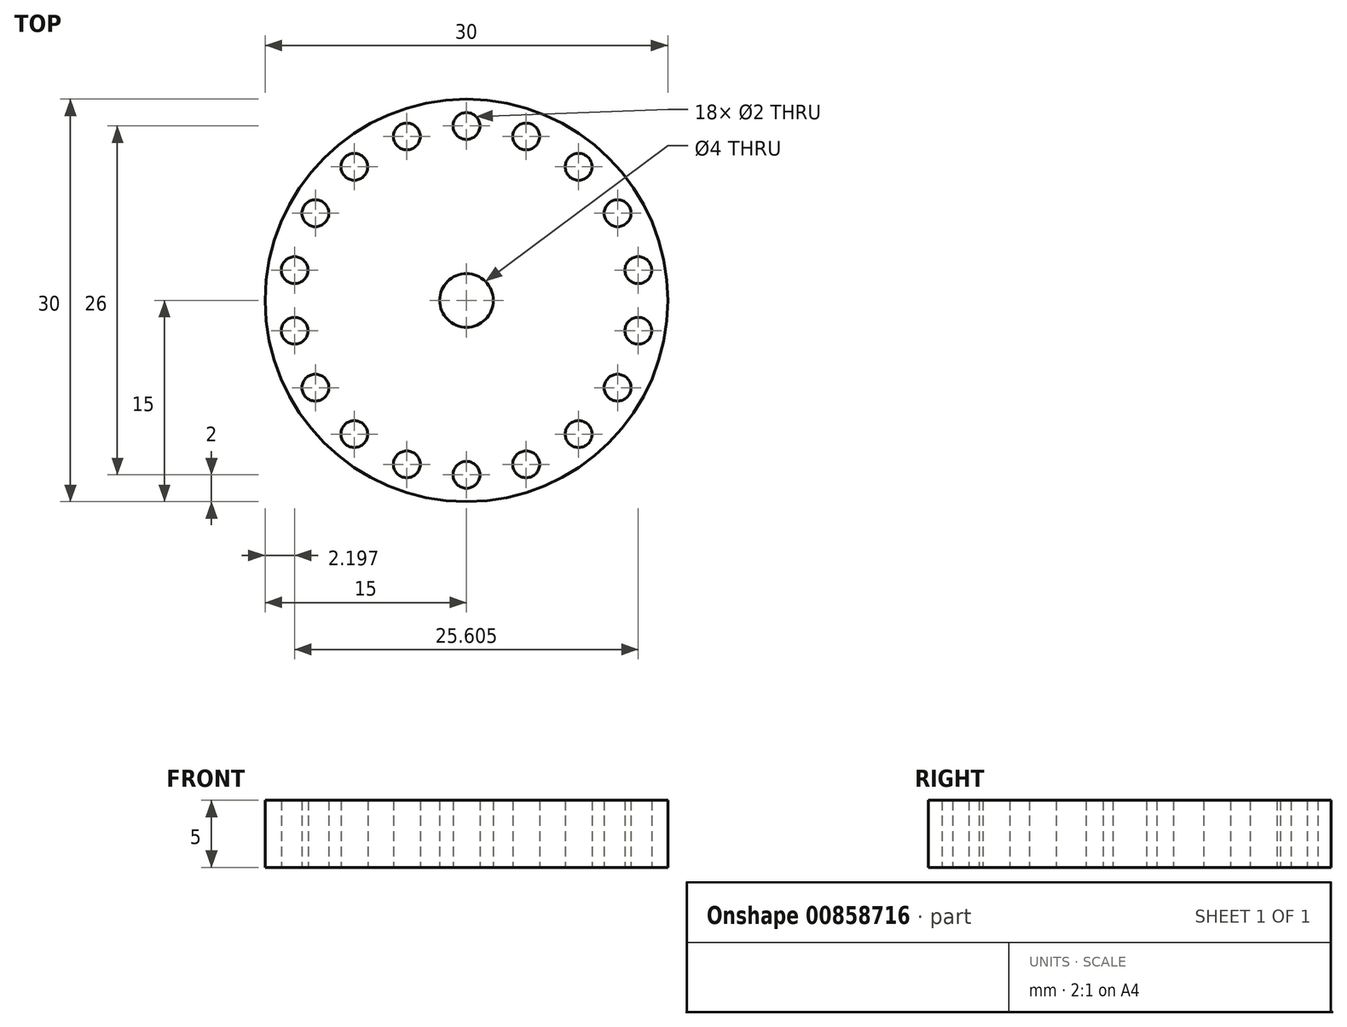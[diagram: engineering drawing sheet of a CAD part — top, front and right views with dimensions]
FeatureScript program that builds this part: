
annotation { "Feature Type Name" : "Feature", "Feature Type Description" : "" }
export const myFeature = defineFeature(function(context is Context, id is Id, definition is map)
    precondition{}
    {
        {
            var Q0;
            Q0=qCreatedBy(makeId("Top.planeOp"),FACE);
            var sketch = newSketch(context, id + "F0", { "sketchPlane" : qUnion([Q0])});
            skCircle(sketch, "E0", {"center": v(0, 0) * mm, "radius": 15 * mm});
            skSolve(sketch);
        }
        {
            var Q0;
            Q0=qCreatedBy(makeId("Top.planeOp"),FACE);
            var sketch = newSketch(context, id + "F1", { "sketchPlane" : qUnion([Q0])});
            skCircle(sketch, "E1", {"center": v(0, 13) * mm, "radius": 1 * mm});
            skCircle(sketch, "E2.1.0", {"center": v(-4.45, 12.22) * mm, "radius": 1 * mm});
            skCircle(sketch, "E2.2.0", {"center": v(-8.36, 9.96) * mm, "radius": 1 * mm});
            skCircle(sketch, "E2.3.0", {"center": v(-11.26, 6.5) * mm, "radius": 1 * mm});
            skCircle(sketch, "E2.4.0", {"center": v(-12.8, 2.26) * mm, "radius": 1 * mm});
            skCircle(sketch, "E2.5.0", {"center": v(-12.8, -2.26) * mm, "radius": 1 * mm});
            skCircle(sketch, "E2.6.0", {"center": v(-11.26, -6.5) * mm, "radius": 1 * mm});
            skCircle(sketch, "E2.7.0", {"center": v(-8.36, -9.96) * mm, "radius": 1 * mm});
            skCircle(sketch, "E2.8.0", {"center": v(-4.45, -12.22) * mm, "radius": 1 * mm});
            skCircle(sketch, "E2.9.0", {"center": v(0, -13) * mm, "radius": 1 * mm});
            skCircle(sketch, "E2.10.0", {"center": v(4.45, -12.22) * mm, "radius": 1 * mm});
            skCircle(sketch, "E2.11.0", {"center": v(8.36, -9.96) * mm, "radius": 1 * mm});
            skCircle(sketch, "E2.12.0", {"center": v(11.26, -6.5) * mm, "radius": 1 * mm});
            skCircle(sketch, "E2.13.0", {"center": v(12.8, -2.26) * mm, "radius": 1 * mm});
            skCircle(sketch, "E2.14.0", {"center": v(12.8, 2.26) * mm, "radius": 1 * mm});
            skCircle(sketch, "E2.15.0", {"center": v(11.26, 6.5) * mm, "radius": 1 * mm});
            skCircle(sketch, "E2.16.0", {"center": v(8.36, 9.96) * mm, "radius": 1 * mm});
            skCircle(sketch, "E2.17.0", {"center": v(4.45, 12.22) * mm, "radius": 1 * mm});
            skPoint(sketch, "E2.center", {"position": v(0, 0) * mm});
            skSolve(sketch);
        }
        {
            var Q0;
            Q0=qCreatedBy(makeId("Top.planeOp"),FACE);
            var sketch = newSketch(context, id + "F2", { "sketchPlane" : qUnion([Q0])});
            skCircle(sketch, "E3", {"center": v(0, 0) * mm, "radius": 2 * mm});
            skSolve(sketch);
        }
        {
            var Q0;
            Q0 = qSketchRegion(id + "F0", true);
            extrude(context, id + "F3", {"entities" : qUnion([Q0]), "depth" : 5 * mm, "offsetDistance" : 25 * mm});
        }
        {
            var Q0;
            Q0 = qSketchRegion(id + "F1", true);
            extrude(context, id + "F4", {"entities" : qUnion([Q0]), "operationType" : NewBodyOperationType.REMOVE, "depth" : 5 * mm, "offsetDistance" : 25 * mm, "hasSecondDirection" : true, "secondDirectionOppositeDirection" : true, "secondDirectionDepth" : 1 * mm});
        }
        {
            var Q0;
            Q0 = qSketchRegion(id + "F2", true);
            extrude(context, id + "F5", {"entities" : qUnion([Q0]), "operationType" : NewBodyOperationType.REMOVE, "depth" : 5 * mm, "offsetDistance" : 25 * mm});
        }
    });
